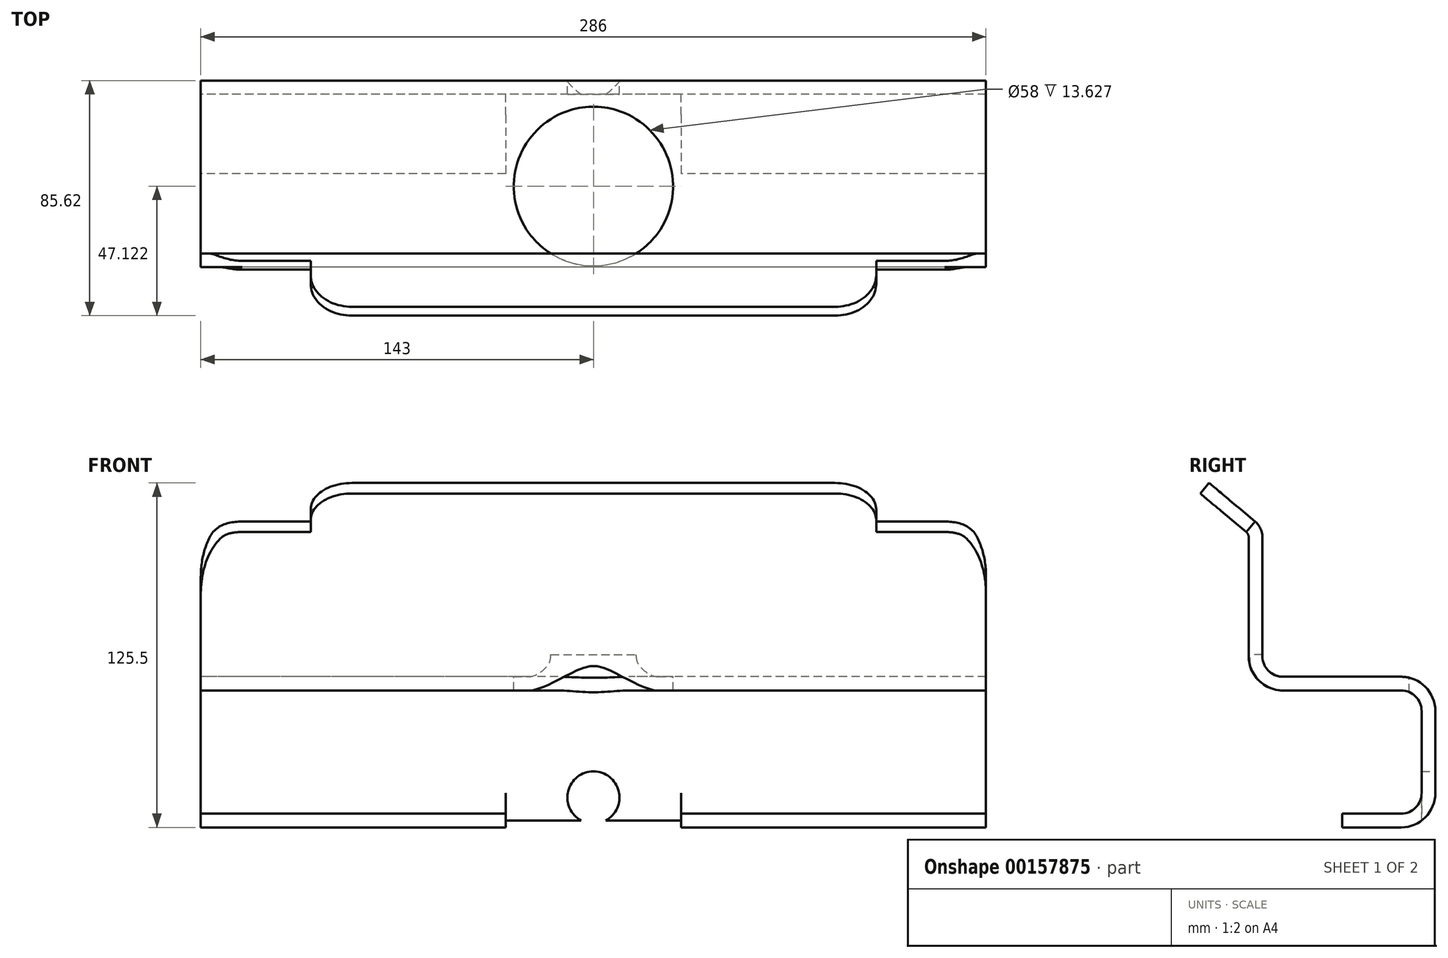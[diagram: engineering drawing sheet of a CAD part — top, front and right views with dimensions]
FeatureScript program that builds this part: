
annotation { "Feature Type Name" : "Feature", "Feature Type Description" : "" }
export const myFeature = defineFeature(function(context is Context, id is Id, definition is map)
    precondition{}
    {
        {
            var Q0;
            Q0=qCreatedBy(makeId("Right.planeOp"),FACE);
            var sketch = newSketch(context, id + "F0", { "sketchPlane" : qUnion([Q0])});
            skArc(sketch, "E0", {"start": v(-37.83, 42.97) * mm, "mid": v(-38.06, 44.03) * mm, "end": v(-38.72, 44.89) * mm});
            skLineSegment(sketch, "E1", {"start": v(-55.45, 58.92) * mm, "end": v(-52.23, 62.75) * mm});
            skArc(sketch, "E2", {"start": v(-32.83, 42.97) * mm, "mid": v(-33.53, 46.14) * mm, "end": v(-35.5, 48.72) * mm});
            skArc(sketch, "E3", {"start": v(-32.83, -0.36) * mm, "mid": v(-30.63, -5.67) * mm, "end": v(-25.33, -7.86) * mm});
            skArc(sketch, "E4", {"start": v(30.17, -20.36) * mm, "mid": v(26.51, -11.52) * mm, "end": v(17.67, -7.86) * mm});
            skLineSegment(sketch, "E5", {"start": v(-3.79, -62.75) * mm, "end": v(-3.79, -57.75) * mm});
            skArc(sketch, "E6", {"start": v(17.67, -57.75) * mm, "mid": v(22.98, -55.55) * mm, "end": v(25.17, -50.25) * mm});
            skArc(sketch, "E7", {"start": v(25.17, -20.36) * mm, "mid": v(22.98, -15.06) * mm, "end": v(17.67, -12.86) * mm});
            skArc(sketch, "E8", {"start": v(-37.83, -0.36) * mm, "mid": v(-34.17, -9.2) * mm, "end": v(-25.33, -12.86) * mm});
            skArc(sketch, "E9", {"start": v(17.67, -62.75) * mm, "mid": v(26.51, -59.09) * mm, "end": v(30.17, -50.25) * mm});
            skLineSegment(sketch, "E10", {"start": v(-35.5, 48.72) * mm, "end": v(-52.23, 62.75) * mm});
            skLineSegment(sketch, "E11", {"start": v(-38.72, 44.89) * mm, "end": v(-55.45, 58.92) * mm});
            skLineSegment(sketch, "E12", {"start": v(-32.83, 42.97) * mm, "end": v(-32.83, -0.36) * mm});
            skLineSegment(sketch, "E13", {"start": v(-37.83, 42.97) * mm, "end": v(-37.83, -0.36) * mm});
            skLineSegment(sketch, "E14", {"start": v(-25.33, -7.86) * mm, "end": v(17.67, -7.86) * mm});
            skLineSegment(sketch, "E15", {"start": v(-25.33, -12.86) * mm, "end": v(17.67, -12.86) * mm});
            skLineSegment(sketch, "E16", {"start": v(30.17, -20.36) * mm, "end": v(30.17, -50.25) * mm});
            skLineSegment(sketch, "E17", {"start": v(25.17, -20.36) * mm, "end": v(25.17, -50.25) * mm});
            skLineSegment(sketch, "E18", {"start": v(17.67, -62.75) * mm, "end": v(-3.79, -62.75) * mm});
            skLineSegment(sketch, "E19", {"start": v(17.67, -57.75) * mm, "end": v(-3.79, -57.75) * mm});
            skLineSegment(sketch, "E20", {"start": v(0, 0) * mm, "end": v(-113.48, 0) * mm, "construction": true});
            skSolve(sketch);
        }
        {
            var Q0;
            Q0=qSketchRegion(id+"F0",true);
            extrude(context, id + "F1", {"entities" : qUnion([Q0]), "endBound" : BoundingType.SYMMETRIC, "depth" : 286 * mm});
        }
        {
            var Q0;
            Q0=qCreatedBy(makeId("Top.planeOp"),FACE);
            var sketch = newSketch(context, id + "F2", { "sketchPlane" : qUnion([Q0])});
            skLineSegment(sketch, "E21.0", {"start": v(143, 30.17) * mm, "end": v(-143, 30.17) * mm, "construction": true});
            skLineSegment(sketch, "E22.0", {"start": v(143, 25.17) * mm, "end": v(-143, 25.17) * mm, "construction": true});
            skLineSegment(sketch, "E23.0", {"start": v(143, -3.79) * mm, "end": v(-143, -3.79) * mm, "construction": true});
            skLineSegment(sketch, "E24.bottom", {"start": v(-346.92, 71.4) * mm, "end": v(-170, 71.4) * mm});
            skLineSegment(sketch, "E24.top", {"start": v(-346.92, -20.36) * mm, "end": v(-170, -20.36) * mm});
            skLineSegment(sketch, "E24.left", {"start": v(-346.92, 71.4) * mm, "end": v(-346.92, -20.36) * mm});
            skLineSegment(sketch, "E24.right", {"start": v(-170, 71.4) * mm, "end": v(-170, -20.36) * mm});
            skLineSegment(sketch, "E25.bottom", {"start": v(170, 71.4) * mm, "end": v(314.46, 71.4) * mm});
            skLineSegment(sketch, "E25.top", {"start": v(170, -22.45) * mm, "end": v(314.46, -22.45) * mm});
            skLineSegment(sketch, "E25.left", {"start": v(170, 71.4) * mm, "end": v(170, -22.45) * mm});
            skLineSegment(sketch, "E25.right", {"start": v(314.46, 71.4) * mm, "end": v(314.46, -22.45) * mm});
            skLineSegment(sketch, "E26", {"start": v(-346.92, 71.4) * mm, "end": v(192.66, 71.4) * mm, "construction": true});
            skSolve(sketch);
        }
        {
            var Q0;
            Q0=makeQuery(id+"F2.imprint","IMPRINT",FACE,{"disambiguationData":[TD([[makeQuery(id+"F2.imprint","IMPRINT",EDGE,{"derivedFrom":sQuery(id+"F2.wireOp",EDGE,"E24.bottom")}),-1.0]])]});
            var Q1;
            Q1=makeQuery(id+"F2.imprint","IMPRINT",FACE,{"disambiguationData":[TD([[makeQuery(id+"F2.imprint","IMPRINT",EDGE,{"derivedFrom":sQuery(id+"F2.wireOp",EDGE,"E25.bottom")}),-1.0]])]});
            extrude(context, id + "F3", {"entities" : qUnion([Q0, Q1]), "operationType" : NewBodyOperationType.REMOVE, "endBound" : BoundingType.SYMMETRIC, "depth" : 200 * mm});
        }
        {
            var Q0;
            Q0=makeQuery(id+"F1.opExtrude","SWEPT_FACE",FACE,{"disambiguationData":[OSD([sQuery(id+"F0.wireOp",EDGE,"E10")])]});
            var sketch = newSketch(context, id + "F4", { "sketchPlane" : qUnion([Q0])});
            skLineSegment(sketch, "E27", {"start": v(247.26, -58.51) * mm, "end": v(103, -58.51) * mm});
            skLineSegment(sketch, "E28", {"start": v(103, -58.51) * mm, "end": v(103, -95.58) * mm});
            skLineSegment(sketch, "E29", {"start": v(103, -95.58) * mm, "end": v(247.26, -95.58) * mm});
            skLineSegment(sketch, "E30", {"start": v(247.26, -58.51) * mm, "end": v(247.26, -95.58) * mm});
            skLineSegment(sketch, "E31", {"start": v(247.26, -95.58) * mm, "end": v(-263.65, -95.58) * mm, "construction": true});
            skLineSegment(sketch, "E32", {"start": v(247.26, -58.51) * mm, "end": v(-263.65, -58.51) * mm, "construction": true});
            skLineSegment(sketch, "E33.bottom", {"start": v(-103, -95.58) * mm, "end": v(-252.3, -95.58) * mm});
            skLineSegment(sketch, "E33.top", {"start": v(-103, -58.51) * mm, "end": v(-252.3, -58.51) * mm});
            skLineSegment(sketch, "E33.left", {"start": v(-103, -95.58) * mm, "end": v(-103, -58.51) * mm});
            skLineSegment(sketch, "E33.right", {"start": v(-252.3, -95.58) * mm, "end": v(-252.3, -58.51) * mm});
            skSolve(sketch);
        }
        {
            var Q0;
            {var subQ1=sQuery(id+"F0.wireOp",EDGE,"E10");var subQ2=makeQuery(id+"F1.opExtrude","CAP_EDGE",EDGE,{"disambiguationData":[OSD([subQ1])],"isStart":false});Q0=makeQuery(id+"F4.imprint","IMPRINT",FACE,{"disambiguationData":[TD([[makeQuery(id+"F4.imprint","IMPRINT",EDGE,{"derivedFrom":subQ2}),-1.0]])]});}
            var Q1;
            {var subQ6=sQuery(id+"F4.wireOp",EDGE,"E29");Q1=makeQuery(id+"F4.imprint","IMPRINT",FACE,{"disambiguationData":[TD([[makeQuery(id+"F4.imprint","IMPRINT",EDGE,{"derivedFrom":subQ6}),1.0]])]});}
            var Q2;
            {var subQ2=sQuery(id+"F4.wireOp",EDGE,"E33.bottom");Q2=makeQuery(id+"F4.imprint","IMPRINT",FACE,{"disambiguationData":[TD([[makeQuery(id+"F4.imprint","IMPRINT",EDGE,{"derivedFrom":subQ2}),-1.0]])]});}
            var Q3;
            {var subQ1=sQuery(id+"F0.wireOp",EDGE,"E10");var subQ2=makeQuery(id+"F1.opExtrude","CAP_EDGE",EDGE,{"disambiguationData":[OSD([subQ1])],"isStart":true});Q3=makeQuery(id+"F4.imprint","IMPRINT",FACE,{"disambiguationData":[TD([[makeQuery(id+"F4.imprint","IMPRINT",EDGE,{"derivedFrom":subQ2}),1.0]])]});}
            extrude(context, id + "F5", {"entities" : qUnion([Q0, Q1, Q2, Q3]), "operationType" : NewBodyOperationType.REMOVE, "endBound" : BoundingType.SYMMETRIC, "oppositeDirection" : true, "depth" : 25 * mm});
        }
        {
            var Q0;
            Q0=makeQuery(id+"F5.boolean.opBoolean","INTERSECT",EDGE,{"derivedFrom":[makeQuery(id+"F1.opExtrude","SWEPT_FACE",FACE,{"disambiguationData":[OSD([sQuery(id+"F0.wireOp",EDGE,"E1")])]}),makeQuery(id+"F5.opExtrude","SWEPT_FACE",FACE,{"disambiguationData":[OSD([sQuery(id+"F4.wireOp",EDGE,"E28")])]})]});
            var Q1;
            Q1=makeQuery(id+"F5.boolean.opBoolean","INTERSECT",EDGE,{"derivedFrom":[makeQuery(id+"F1.opExtrude","SWEPT_FACE",FACE,{"disambiguationData":[OSD([sQuery(id+"F0.wireOp",EDGE,"E1")])]}),makeQuery(id+"F5.opExtrude","SWEPT_FACE",FACE,{"disambiguationData":[OSD([sQuery(id+"F4.wireOp",EDGE,"E33.left")])]})]});
            var Q2;
            Q2=makeQuery(id+"F5.boolean.opBoolean","INTERSECT",EDGE,{"derivedFrom":[makeQuery(id+"F1.opExtrude","CAP_FACE",FACE,{"disambiguationData":[OSD([sQuery(id+"F0.wireOp",EDGE,"E0"),sQuery(id+"F0.wireOp",EDGE,"E1"),sQuery(id+"F0.wireOp",EDGE,"E2"),sQuery(id+"F0.wireOp",EDGE,"E3"),sQuery(id+"F0.wireOp",EDGE,"E4"),sQuery(id+"F0.wireOp",EDGE,"E5"),sQuery(id+"F0.wireOp",EDGE,"E6"),sQuery(id+"F0.wireOp",EDGE,"E7"),sQuery(id+"F0.wireOp",EDGE,"E8"),sQuery(id+"F0.wireOp",EDGE,"E9"),sQuery(id+"F0.wireOp",EDGE,"E10"),sQuery(id+"F0.wireOp",EDGE,"E11"),sQuery(id+"F0.wireOp",EDGE,"E12"),sQuery(id+"F0.wireOp",EDGE,"E13"),sQuery(id+"F0.wireOp",EDGE,"E14"),sQuery(id+"F0.wireOp",EDGE,"E15"),sQuery(id+"F0.wireOp",EDGE,"E16"),sQuery(id+"F0.wireOp",EDGE,"E17"),sQuery(id+"F0.wireOp",EDGE,"E18"),sQuery(id+"F0.wireOp",EDGE,"E19")])],"isStart":true}),makeQuery(id+"F5.opExtrude","SWEPT_FACE",FACE,{"disambiguationData":[OSD([sQuery(id+"F4.wireOp",EDGE,"E33.top")])]})]});
            var Q3;
            Q3=makeQuery(id+"F5.boolean.opBoolean","INTERSECT",EDGE,{"derivedFrom":[makeQuery(id+"F1.opExtrude","CAP_FACE",FACE,{"disambiguationData":[OSD([sQuery(id+"F0.wireOp",EDGE,"E0"),sQuery(id+"F0.wireOp",EDGE,"E1"),sQuery(id+"F0.wireOp",EDGE,"E2"),sQuery(id+"F0.wireOp",EDGE,"E3"),sQuery(id+"F0.wireOp",EDGE,"E4"),sQuery(id+"F0.wireOp",EDGE,"E5"),sQuery(id+"F0.wireOp",EDGE,"E6"),sQuery(id+"F0.wireOp",EDGE,"E7"),sQuery(id+"F0.wireOp",EDGE,"E8"),sQuery(id+"F0.wireOp",EDGE,"E9"),sQuery(id+"F0.wireOp",EDGE,"E10"),sQuery(id+"F0.wireOp",EDGE,"E11"),sQuery(id+"F0.wireOp",EDGE,"E12"),sQuery(id+"F0.wireOp",EDGE,"E13"),sQuery(id+"F0.wireOp",EDGE,"E14"),sQuery(id+"F0.wireOp",EDGE,"E15"),sQuery(id+"F0.wireOp",EDGE,"E16"),sQuery(id+"F0.wireOp",EDGE,"E17"),sQuery(id+"F0.wireOp",EDGE,"E18"),sQuery(id+"F0.wireOp",EDGE,"E19")])],"isStart":false}),makeQuery(id+"F5.opExtrude","SWEPT_FACE",FACE,{"disambiguationData":[OSD([sQuery(id+"F4.wireOp",EDGE,"E27")])]})]});
            fillet(context, id + "F6", {"entities" : qUnion([Q0, Q1, Q2, Q3]), "radius" : 15 * mm, "tangentPropagation" : true, "allowEdgeOverflow" : false});
        }
        {
            var Q0;
            Q0=makeQuery(id+"F1.opExtrude","SWEPT_FACE",FACE,{"disambiguationData":[OSD([sQuery(id+"F0.wireOp",EDGE,"E18")])]});
            var sketch = newSketch(context, id + "F7", { "sketchPlane" : qUnion([Q0])});
            skLineSegment(sketch, "E34.bottom", {"start": v(32, -25.17) * mm, "end": v(-32, -25.17) * mm});
            skLineSegment(sketch, "E34.top", {"start": v(32, 15.24) * mm, "end": v(-32, 15.24) * mm});
            skLineSegment(sketch, "E34.left", {"start": v(32, -25.17) * mm, "end": v(32, 15.24) * mm});
            skLineSegment(sketch, "E34.right", {"start": v(-32, -25.17) * mm, "end": v(-32, 15.24) * mm});
            skSolve(sketch);
        }
        {
            var Q0;
            {var subQ0=sQuery(id+"F7.wireOp",EDGE,"E34.bottom");Q0=makeQuery(id+"F7.imprint","IMPRINT",FACE,{"disambiguationData":[TD([[makeQuery(id+"F7.imprint","IMPRINT",EDGE,{"derivedFrom":subQ0}),-1.0]])]});}
            var Q1;
            {var subQ0=sQuery(id+"F7.wireOp",EDGE,"E34.top");Q1=makeQuery(id+"F7.imprint","IMPRINT",FACE,{"disambiguationData":[TD([[makeQuery(id+"F7.imprint","IMPRINT",EDGE,{"derivedFrom":subQ0}),1.0]])]});}
            var Q2;
            {var subQ0=sQuery(id+"F7.wireOp",EDGE,"E34.left");var subQ1=sQuery(id+"F0.wireOp",EDGE,"E18");var subQ2=makeQuery(id+"F1.opExtrude","SWEPT_EDGE",EDGE,{"disambiguationData":[OSD([sQuery(id+"F0.wireOp",EDGE,"E9"),subQ1])]});var subQ3=makeQuery(id+"F7.imprint","INTERSECT",VERTEX,{"derivedFrom":[subQ2,subQ0]});Q2=makeQuery(id+"F7.imprint","IMPRINT",FACE,{"disambiguationData":[TD([[makeQuery(id+"F7.imprint","IMPRINT",EDGE,{"disambiguationData":[TD([[subQ3,-1.0]])],"derivedFrom":subQ0}),1.0]])]});}
            extrude(context, id + "F8", {"entities" : qUnion([Q0, Q1, Q2]), "operationType" : NewBodyOperationType.REMOVE, "oppositeDirection" : true, "depth" : 25 * mm});
        }
        {
            var Q0;
            Q0=makeQuery(id+"F1.opExtrude","SWEPT_FACE",FACE,{"disambiguationData":[OSD([sQuery(id+"F0.wireOp",EDGE,"E14")])]});
            var sketch = newSketch(context, id + "F9", { "sketchPlane" : qUnion([Q0])});
            skCircle(sketch, "E35", {"center": v(0, -8.33) * mm, "radius": 29 * mm});
            skSolve(sketch);
        }
        {
            var Q0;
            Q0=qSketchRegion(id+"F9",true);
            extrude(context, id + "F10", {"entities" : qUnion([Q0]), "operationType" : NewBodyOperationType.REMOVE, "oppositeDirection" : true, "depth" : 6 * mm, "hasSecondDirection" : true, "secondDirectionOppositeDirection" : false, "secondDirectionDepth" : 8 * mm});
        }
        {
            var Q0;
            Q0=makeQuery(id+"F1.opExtrude","SWEPT_FACE",FACE,{"disambiguationData":[OSD([sQuery(id+"F0.wireOp",EDGE,"E16")])]});
            var sketch = newSketch(context, id + "F11", { "sketchPlane" : qUnion([Q0])});
            skCircle(sketch, "E36", {"center": v(0, -51.86) * mm, "radius": 9.5 * mm});
            skPoint(sketch, "E37", {"position": v(0, -20.36) * mm});
            skSolve(sketch);
        }
        {
            var Q0;
            Q0=qSketchRegion(id+"F11",true);
            extrude(context, id + "F12", {"entities" : qUnion([Q0]), "operationType" : NewBodyOperationType.REMOVE, "oppositeDirection" : true, "depth" : 25 * mm});
        }
    });
